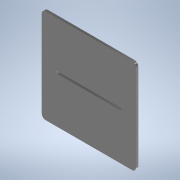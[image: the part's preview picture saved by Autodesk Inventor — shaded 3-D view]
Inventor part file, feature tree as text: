
AUTODESK INVENTOR PART (.ipt)
format: ipt  version: 2020 (Build 240168000, 168)  size: 113,152 bytes
history: native  units: mm
features: sheet_metal_op x1, sketch x1, other x1
ambient origin geometry x8: Origin, YZ Plane, XZ Plane, XY Plane, X Axis, Y Axis, Z Axis, Center Point
bodies: Solid1 (feature_tree)
feature tree (3):
  sheet_metal_op  "Face1"
  sketch  "Sketch1"  dims[d0=12.0mm d1=12.0mm d2=4.0mm d3=0.3mm d4=0.5mm d5=0.3mm]
  other  "Plate1"
